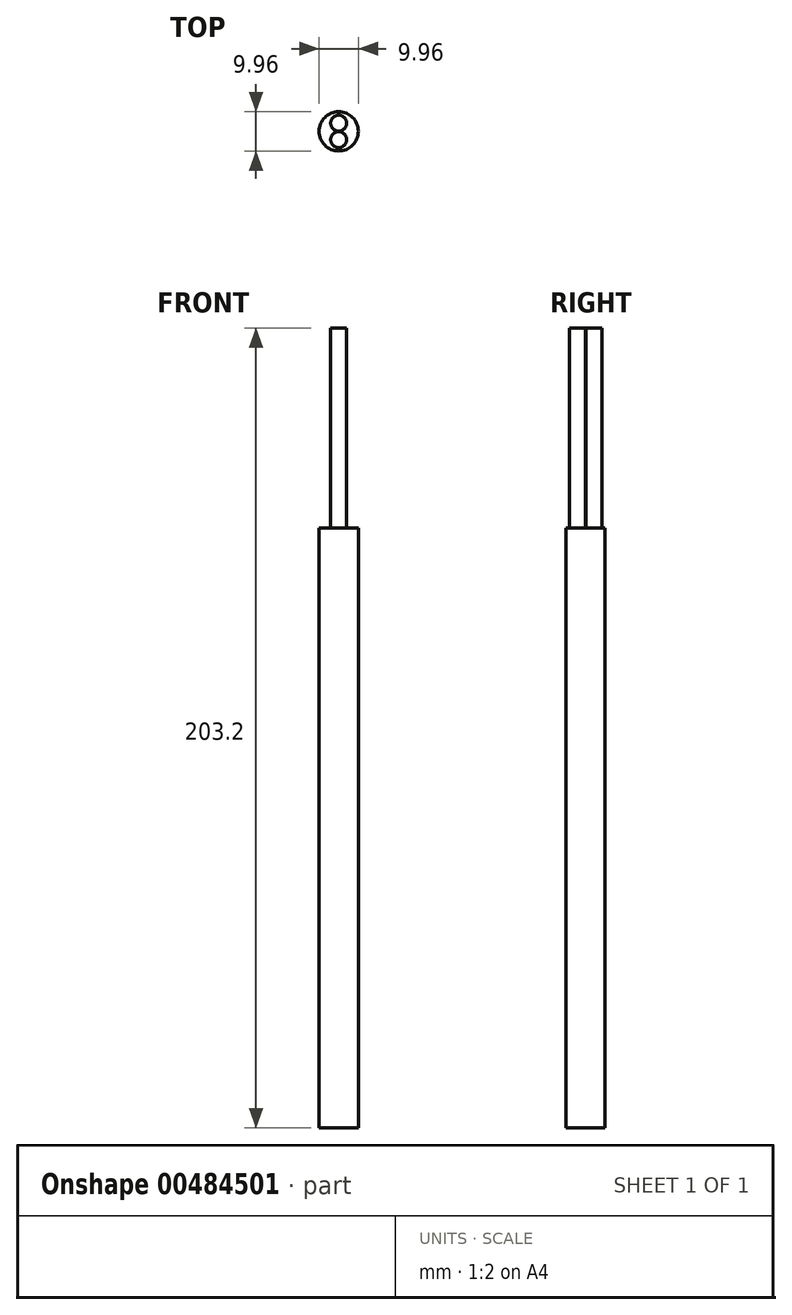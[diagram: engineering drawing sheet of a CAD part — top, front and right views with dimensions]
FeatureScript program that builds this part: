
annotation { "Feature Type Name" : "Feature", "Feature Type Description" : "" }
export const myFeature = defineFeature(function(context is Context, id is Id, definition is map)
    precondition{}
    {
        {
            var Q0;
            Q0=qCreatedBy(makeId("Top.planeOp"),FACE);
            var sketch = newSketch(context, id + "F0", { "sketchPlane" : qUnion([Q0])});
            skCircle(sketch, "E0", {"center": v(0, 0) * mm, "radius": 4.98 * mm});
            skSolve(sketch);
        }
        {
            var Q0;
            Q0 = qSketchRegion(id + "F0", true);
            extrude(context, id + "F1", {"entities" : qUnion([Q0]), "depth" : 152.4 * mm});
        }
        {
            var Q0;
            Q0=makeQuery(id+"F1.opExtrude","CAP_FACE",FACE,{"disambiguationData":[OSD([sQuery(id+"F0.wireOp",EDGE,"E0")])],"isStart":false});
            var sketch = newSketch(context, id + "F2", { "sketchPlane" : qUnion([Q0])});
            skCircle(sketch, "E1", {"center": v(0, 2.1) * mm, "radius": 2.03 * mm});
            skCircle(sketch, "E2", {"center": v(0, -2.1) * mm, "radius": 2.03 * mm});
            skLineSegment(sketch, "E3", {"start": v(0, 2.1) * mm, "end": v(0, -2.1) * mm, "construction": true});
            skSolve(sketch);
        }
        {
            var Q0;
            Q0 = qSketchRegion(id + "F2", true);
            extrude(context, id + "F3", {"entities" : qUnion([Q0]), "operationType" : NewBodyOperationType.ADD, "depth" : 50.8 * mm});
        }
    });
